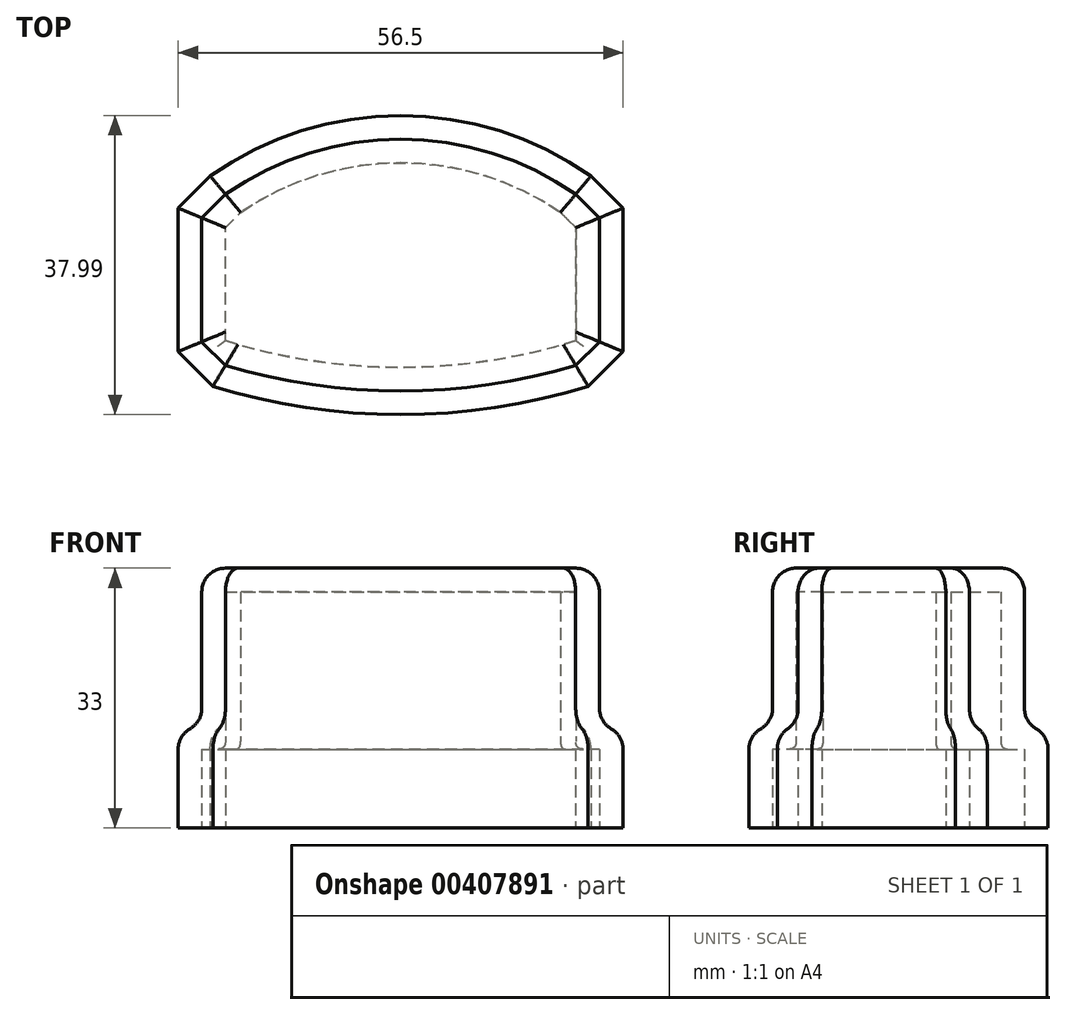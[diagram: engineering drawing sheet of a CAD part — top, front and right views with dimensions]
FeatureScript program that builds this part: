
annotation { "Feature Type Name" : "Feature", "Feature Type Description" : "" }
export const myFeature = defineFeature(function(context is Context, id is Id, definition is map)
    precondition{}
    {
        {
            var Q0;
            Q0=qCreatedBy(makeId("Top.planeOp"),FACE);
            var sketch = newSketch(context, id + "F0", { "sketchPlane" : qUnion([Q0])});
            skLineSegment(sketch, "E0.left", {"start": v(-25.25, -1.8) * mm, "end": v(-25.25, 13.94) * mm});
            skLineSegment(sketch, "E0.right", {"start": v(25.25, -1.8) * mm, "end": v(25.25, 13.94) * mm});
            skLineSegment(sketch, "E1", {"start": v(25.25, 13.94) * mm, "end": v(22.24, 16.95) * mm});
            skLineSegment(sketch, "E2", {"start": v(25.25, -1.8) * mm, "end": v(22.24, -4.8) * mm});
            skLineSegment(sketch, "E3", {"start": v(-25.25, 13.94) * mm, "end": v(-22.24, 16.95) * mm});
            skLineSegment(sketch, "E4", {"start": v(-25.25, -1.8) * mm, "end": v(-22.24, -4.8) * mm});
            skArc(sketch, "E5", {"start": v(22.24, 16.95) * mm, "mid": v(0, 23.94) * mm, "end": v(-22.24, 16.95) * mm});
            skArc(sketch, "E6", {"start": v(-22.24, -4.8) * mm, "mid": v(0, -8.05) * mm, "end": v(22.24, -4.8) * mm});
            skLineSegment(sketch, "E7", {"start": v(-25.25, -1.8) * mm, "end": v(25.25, -1.8) * mm, "construction": true});
            skLineSegment(sketch, "E8", {"start": v(-25.25, 13.94) * mm, "end": v(25.25, 13.94) * mm, "construction": true});
            skLineSegment(sketch, "E9.0", {"start": v(28.25, 15.19) * mm, "end": v(24.18, 19.25) * mm});
            skLineSegment(sketch, "E9.1", {"start": v(28.25, -3.04) * mm, "end": v(28.25, 15.19) * mm});
            skArc(sketch, "E9.2", {"start": v(24.18, 19.25) * mm, "mid": v(0, 26.94) * mm, "end": v(-24.18, 19.25) * mm});
            skLineSegment(sketch, "E9.3", {"start": v(28.25, -3.04) * mm, "end": v(23.83, -7.45) * mm});
            skLineSegment(sketch, "E9.4", {"start": v(-28.25, 15.19) * mm, "end": v(-24.18, 19.25) * mm});
            skLineSegment(sketch, "E9.5", {"start": v(-28.25, -3.04) * mm, "end": v(-28.25, 15.19) * mm});
            skLineSegment(sketch, "E9.6", {"start": v(-28.25, -3.04) * mm, "end": v(-23.83, -7.45) * mm});
            skArc(sketch, "E9.7", {"start": v(-23.83, -7.45) * mm, "mid": v(0, -11.05) * mm, "end": v(23.83, -7.45) * mm});
            skLineSegment(sketch, "E10.0", {"start": v(22.25, 12.7) * mm, "end": v(20.31, 14.64) * mm});
            skLineSegment(sketch, "E10.1", {"start": v(-22.25, 12.7) * mm, "end": v(-20.31, 14.64) * mm});
            skLineSegment(sketch, "E10.2", {"start": v(-22.25, -1.66) * mm, "end": v(-22.25, 12.7) * mm});
            skArc(sketch, "E10.3", {"start": v(20.31, 14.64) * mm, "mid": v(0, 20.94) * mm, "end": v(-20.31, 14.64) * mm});
            skArc(sketch, "E10.4", {"start": v(-22.25, -1.66) * mm, "mid": v(0, -5.05) * mm, "end": v(22.25, -1.66) * mm});
            skLineSegment(sketch, "E10.5", {"start": v(22.25, -1.66) * mm, "end": v(22.25, 12.7) * mm});
            skSolve(sketch);
        }
        {
            var Q0;
            Q0=makeQuery(id+"F0.imprint","IMPRINT",FACE,{"disambiguationData":[TD([[makeQuery(id+"F0.imprint","IMPRINT",EDGE,{"derivedFrom":sQuery(id+"F0.wireOp",EDGE,"E0.left")}),1.0]])]});
            extrude(context, id + "F1", {"entities" : qUnion([Q0]), "depth" : 13 * mm});
        }
        {
            var Q0;
            Q0=makeQuery(id+"F0.imprint","IMPRINT",FACE,{"disambiguationData":[TD([[makeQuery(id+"F0.imprint","IMPRINT",EDGE,{"derivedFrom":sQuery(id+"F0.wireOp",EDGE,"E0.left")}),-1.0]])]});
            var Q1;
            Q1=makeQuery(id+"F0.imprint","IMPRINT",FACE,{"disambiguationData":[TD([[makeQuery(id+"F0.imprint","IMPRINT",EDGE,{"derivedFrom":sQuery(id+"F0.wireOp",EDGE,"E10.0")}),1.0]])]});
            extrude(context, id + "F2", {"entities" : qUnion([Q0, Q1]), "operationType" : NewBodyOperationType.ADD, "depth" : 33 * mm});
        }
        {
            var Q0;
            Q0=makeQuery(id+"F0.imprint","IMPRINT",FACE,{"disambiguationData":[TD([[makeQuery(id+"F0.imprint","IMPRINT",EDGE,{"derivedFrom":sQuery(id+"F0.wireOp",EDGE,"E10.0")}),1.0]])]});
            var Q1;
            Q1=makeQuery(id+"F0.imprint","IMPRINT",FACE,{"disambiguationData":[TD([[makeQuery(id+"F0.imprint","IMPRINT",EDGE,{"derivedFrom":sQuery(id+"F0.wireOp",EDGE,"E0.left")}),-1.0]])]});
            extrude(context, id + "F3", {"entities" : qUnion([Q0, Q1]), "operationType" : NewBodyOperationType.REMOVE, "depth" : 10 * mm});
        }
        {
            var Q0;
            Q0=makeQuery(id+"F0.imprint","IMPRINT",FACE,{"disambiguationData":[TD([[makeQuery(id+"F0.imprint","IMPRINT",EDGE,{"derivedFrom":sQuery(id+"F0.wireOp",EDGE,"E10.0")}),1.0]])]});
            extrude(context, id + "F4", {"entities" : qUnion([Q0]), "operationType" : NewBodyOperationType.REMOVE, "depth" : 30 * mm});
        }
        {
            var Q0;
            Q0=makeQuery(id+"F1.opExtrude","CAP_EDGE",EDGE,{"disambiguationData":[OSD([sQuery(id+"F0.wireOp",EDGE,"E9.2")])],"isStart":false});
            var Q1;
            Q1=makeQuery(id+"F1.opExtrude","CAP_EDGE",EDGE,{"disambiguationData":[OSD([sQuery(id+"F0.wireOp",EDGE,"E9.4")])],"isStart":false});
            var Q2;
            Q2=makeQuery(id+"F1.opExtrude","CAP_EDGE",EDGE,{"disambiguationData":[OSD([sQuery(id+"F0.wireOp",EDGE,"E9.5")])],"isStart":false});
            var Q3;
            Q3=makeQuery(id+"F1.opExtrude","CAP_EDGE",EDGE,{"disambiguationData":[OSD([sQuery(id+"F0.wireOp",EDGE,"E9.6")])],"isStart":false});
            var Q4;
            Q4=makeQuery(id+"F1.opExtrude","CAP_EDGE",EDGE,{"disambiguationData":[OSD([sQuery(id+"F0.wireOp",EDGE,"E9.7")])],"isStart":false});
            var Q5;
            Q5=makeQuery(id+"F1.opExtrude","CAP_EDGE",EDGE,{"disambiguationData":[OSD([sQuery(id+"F0.wireOp",EDGE,"E9.0")])],"isStart":false});
            var Q6;
            Q6=makeQuery(id+"F1.opExtrude","CAP_EDGE",EDGE,{"disambiguationData":[OSD([sQuery(id+"F0.wireOp",EDGE,"E9.1")])],"isStart":false});
            var Q7;
            Q7=makeQuery(id+"F1.opExtrude","CAP_EDGE",EDGE,{"disambiguationData":[OSD([sQuery(id+"F0.wireOp",EDGE,"E9.3")])],"isStart":false});
            fillet(context, id + "F5", {"entities" : qUnion([Q0, Q1, Q2, Q3, Q4, Q5, Q6, Q7]), "radius" : 3 * mm, "tangentPropagation" : true, "allowEdgeOverflow" : false});
        }
        {
            var Q0;
            Q0=makeQuery(id+"F5.opFillet","BLEND_EDGE",EDGE,{"blendedFrom":[makeQuery(id+"F1.opExtrude","CAP_EDGE",EDGE,{"disambiguationData":[OSD([sQuery(id+"F0.wireOp",EDGE,"E9.7")])],"isStart":false}),makeQuery(id+"F2.opExtrude","SWEPT_FACE",FACE,{"disambiguationData":[OSD([sQuery(id+"F0.wireOp",EDGE,"E6")])]})],"blendedInto":[makeQuery(id+"F2.opExtrude","SWEPT_FACE",FACE,{"disambiguationData":[OSD([sQuery(id+"F0.wireOp",EDGE,"E6")])]})]});
            var Q1;
            Q1=makeQuery(id+"F5.opFillet","BLEND_EDGE",EDGE,{"blendedFrom":[makeQuery(id+"F1.opExtrude","CAP_EDGE",EDGE,{"disambiguationData":[OSD([sQuery(id+"F0.wireOp",EDGE,"E9.6")])],"isStart":false}),makeQuery(id+"F2.opExtrude","SWEPT_FACE",FACE,{"disambiguationData":[OSD([sQuery(id+"F0.wireOp",EDGE,"E4")])]})],"blendedInto":[makeQuery(id+"F2.opExtrude","SWEPT_FACE",FACE,{"disambiguationData":[OSD([sQuery(id+"F0.wireOp",EDGE,"E4")])]})]});
            var Q2;
            Q2=makeQuery(id+"F5.opFillet","BLEND_EDGE",EDGE,{"blendedFrom":[makeQuery(id+"F1.opExtrude","CAP_EDGE",EDGE,{"disambiguationData":[OSD([sQuery(id+"F0.wireOp",EDGE,"E9.5")])],"isStart":false}),makeQuery(id+"F2.opExtrude","SWEPT_FACE",FACE,{"disambiguationData":[OSD([sQuery(id+"F0.wireOp",EDGE,"E0.left")])]})],"blendedInto":[makeQuery(id+"F2.opExtrude","SWEPT_FACE",FACE,{"disambiguationData":[OSD([sQuery(id+"F0.wireOp",EDGE,"E0.left")])]})]});
            var Q3;
            Q3=makeQuery(id+"F5.opFillet","BLEND_EDGE",EDGE,{"blendedFrom":[makeQuery(id+"F1.opExtrude","CAP_EDGE",EDGE,{"disambiguationData":[OSD([sQuery(id+"F0.wireOp",EDGE,"E9.3")])],"isStart":false}),makeQuery(id+"F2.opExtrude","SWEPT_FACE",FACE,{"disambiguationData":[OSD([sQuery(id+"F0.wireOp",EDGE,"E2")])]})],"blendedInto":[makeQuery(id+"F2.opExtrude","SWEPT_FACE",FACE,{"disambiguationData":[OSD([sQuery(id+"F0.wireOp",EDGE,"E2")])]})]});
            var Q4;
            Q4=makeQuery(id+"F5.opFillet","BLEND_EDGE",EDGE,{"blendedFrom":[makeQuery(id+"F1.opExtrude","CAP_EDGE",EDGE,{"disambiguationData":[OSD([sQuery(id+"F0.wireOp",EDGE,"E9.1")])],"isStart":false}),makeQuery(id+"F2.opExtrude","SWEPT_FACE",FACE,{"disambiguationData":[OSD([sQuery(id+"F0.wireOp",EDGE,"E0.right")])]})],"blendedInto":[makeQuery(id+"F2.opExtrude","SWEPT_FACE",FACE,{"disambiguationData":[OSD([sQuery(id+"F0.wireOp",EDGE,"E0.right")])]})]});
            var Q5;
            Q5=makeQuery(id+"F5.opFillet","BLEND_EDGE",EDGE,{"blendedFrom":[makeQuery(id+"F1.opExtrude","CAP_EDGE",EDGE,{"disambiguationData":[OSD([sQuery(id+"F0.wireOp",EDGE,"E9.0")])],"isStart":false}),makeQuery(id+"F2.opExtrude","SWEPT_FACE",FACE,{"disambiguationData":[OSD([sQuery(id+"F0.wireOp",EDGE,"E1")])]})],"blendedInto":[makeQuery(id+"F2.opExtrude","SWEPT_FACE",FACE,{"disambiguationData":[OSD([sQuery(id+"F0.wireOp",EDGE,"E1")])]})]});
            var Q6;
            Q6=makeQuery(id+"F5.opFillet","BLEND_EDGE",EDGE,{"blendedFrom":[makeQuery(id+"F1.opExtrude","CAP_EDGE",EDGE,{"disambiguationData":[OSD([sQuery(id+"F0.wireOp",EDGE,"E9.2")])],"isStart":false}),makeQuery(id+"F2.opExtrude","SWEPT_FACE",FACE,{"disambiguationData":[OSD([sQuery(id+"F0.wireOp",EDGE,"E5")])]})],"blendedInto":[makeQuery(id+"F2.opExtrude","SWEPT_FACE",FACE,{"disambiguationData":[OSD([sQuery(id+"F0.wireOp",EDGE,"E5")])]})]});
            var Q7;
            Q7=makeQuery(id+"F5.opFillet","BLEND_EDGE",EDGE,{"blendedFrom":[makeQuery(id+"F1.opExtrude","CAP_EDGE",EDGE,{"disambiguationData":[OSD([sQuery(id+"F0.wireOp",EDGE,"E9.4")])],"isStart":false}),makeQuery(id+"F2.opExtrude","SWEPT_FACE",FACE,{"disambiguationData":[OSD([sQuery(id+"F0.wireOp",EDGE,"E3")])]})],"blendedInto":[makeQuery(id+"F2.opExtrude","SWEPT_FACE",FACE,{"disambiguationData":[OSD([sQuery(id+"F0.wireOp",EDGE,"E3")])]})]});
            fillet(context, id + "F6", {"entities" : qUnion([Q0, Q1, Q2, Q3, Q4, Q5, Q6, Q7]), "radius" : 3 * mm, "tangentPropagation" : true, "allowEdgeOverflow" : false});
        }
        {
            var Q0;
            Q0=makeQuery(id+"F2.opExtrude","CAP_EDGE",EDGE,{"disambiguationData":[OSD([sQuery(id+"F0.wireOp",EDGE,"E6")])],"isStart":false});
            var Q1;
            Q1=makeQuery(id+"F2.opExtrude","CAP_FACE",FACE,{"disambiguationData":[OSD([sQuery(id+"F0.wireOp",EDGE,"E0.left"),sQuery(id+"F0.wireOp",EDGE,"E0.right"),sQuery(id+"F0.wireOp",EDGE,"E1"),sQuery(id+"F0.wireOp",EDGE,"E2"),sQuery(id+"F0.wireOp",EDGE,"E3"),sQuery(id+"F0.wireOp",EDGE,"E4"),sQuery(id+"F0.wireOp",EDGE,"E5"),sQuery(id+"F0.wireOp",EDGE,"E6")])],"isStart":false});
            fillet(context, id + "F7", {"entities" : qUnion([Q0, Q1]), "radius" : 3 * mm, "tangentPropagation" : true, "allowEdgeOverflow" : false});
        }
        {
            var Q0;
            Q0=makeQuery(id+"F4.boolean.opBoolean","INTERSECT",EDGE,{"derivedFrom":[makeQuery(id+"F3.boolean.opBoolean","COPY",FACE,{"derivedFrom":makeQuery(id+"F3.opExtrude","CAP_FACE",FACE,{"disambiguationData":[OSD([sQuery(id+"F0.wireOp",EDGE,"E0.left"),sQuery(id+"F0.wireOp",EDGE,"E0.right"),sQuery(id+"F0.wireOp",EDGE,"E1"),sQuery(id+"F0.wireOp",EDGE,"E2"),sQuery(id+"F0.wireOp",EDGE,"E3"),sQuery(id+"F0.wireOp",EDGE,"E4"),sQuery(id+"F0.wireOp",EDGE,"E5"),sQuery(id+"F0.wireOp",EDGE,"E6")])],"isStart":false})}),makeQuery(id+"F4.opExtrude","SWEPT_FACE",FACE,{"disambiguationData":[OSD([sQuery(id+"F0.wireOp",EDGE,"E10.5")])]})]});
            var Q1;
            Q1=makeQuery(id+"F4.boolean.opBoolean","INTERSECT",EDGE,{"derivedFrom":[makeQuery(id+"F3.boolean.opBoolean","COPY",FACE,{"derivedFrom":makeQuery(id+"F3.opExtrude","CAP_FACE",FACE,{"disambiguationData":[OSD([sQuery(id+"F0.wireOp",EDGE,"E0.left"),sQuery(id+"F0.wireOp",EDGE,"E0.right"),sQuery(id+"F0.wireOp",EDGE,"E1"),sQuery(id+"F0.wireOp",EDGE,"E2"),sQuery(id+"F0.wireOp",EDGE,"E3"),sQuery(id+"F0.wireOp",EDGE,"E4"),sQuery(id+"F0.wireOp",EDGE,"E5"),sQuery(id+"F0.wireOp",EDGE,"E6")])],"isStart":false})}),makeQuery(id+"F4.opExtrude","SWEPT_FACE",FACE,{"disambiguationData":[OSD([sQuery(id+"F0.wireOp",EDGE,"E10.0")])]})]});
            var Q2;
            Q2=makeQuery(id+"F4.boolean.opBoolean","INTERSECT",EDGE,{"derivedFrom":[makeQuery(id+"F3.boolean.opBoolean","COPY",FACE,{"derivedFrom":makeQuery(id+"F3.opExtrude","CAP_FACE",FACE,{"disambiguationData":[OSD([sQuery(id+"F0.wireOp",EDGE,"E0.left"),sQuery(id+"F0.wireOp",EDGE,"E0.right"),sQuery(id+"F0.wireOp",EDGE,"E1"),sQuery(id+"F0.wireOp",EDGE,"E2"),sQuery(id+"F0.wireOp",EDGE,"E3"),sQuery(id+"F0.wireOp",EDGE,"E4"),sQuery(id+"F0.wireOp",EDGE,"E5"),sQuery(id+"F0.wireOp",EDGE,"E6")])],"isStart":false})}),makeQuery(id+"F4.opExtrude","SWEPT_FACE",FACE,{"disambiguationData":[OSD([sQuery(id+"F0.wireOp",EDGE,"E10.3")])]})]});
            var Q3;
            Q3=makeQuery(id+"F4.boolean.opBoolean","INTERSECT",EDGE,{"derivedFrom":[makeQuery(id+"F3.boolean.opBoolean","COPY",FACE,{"derivedFrom":makeQuery(id+"F3.opExtrude","CAP_FACE",FACE,{"disambiguationData":[OSD([sQuery(id+"F0.wireOp",EDGE,"E0.left"),sQuery(id+"F0.wireOp",EDGE,"E0.right"),sQuery(id+"F0.wireOp",EDGE,"E1"),sQuery(id+"F0.wireOp",EDGE,"E2"),sQuery(id+"F0.wireOp",EDGE,"E3"),sQuery(id+"F0.wireOp",EDGE,"E4"),sQuery(id+"F0.wireOp",EDGE,"E5"),sQuery(id+"F0.wireOp",EDGE,"E6")])],"isStart":false})}),makeQuery(id+"F4.opExtrude","SWEPT_FACE",FACE,{"disambiguationData":[OSD([sQuery(id+"F0.wireOp",EDGE,"E10.1")])]})]});
            var Q4;
            Q4=makeQuery(id+"F4.boolean.opBoolean","INTERSECT",EDGE,{"derivedFrom":[makeQuery(id+"F3.boolean.opBoolean","COPY",FACE,{"derivedFrom":makeQuery(id+"F3.opExtrude","CAP_FACE",FACE,{"disambiguationData":[OSD([sQuery(id+"F0.wireOp",EDGE,"E0.left"),sQuery(id+"F0.wireOp",EDGE,"E0.right"),sQuery(id+"F0.wireOp",EDGE,"E1"),sQuery(id+"F0.wireOp",EDGE,"E2"),sQuery(id+"F0.wireOp",EDGE,"E3"),sQuery(id+"F0.wireOp",EDGE,"E4"),sQuery(id+"F0.wireOp",EDGE,"E5"),sQuery(id+"F0.wireOp",EDGE,"E6")])],"isStart":false})}),makeQuery(id+"F4.opExtrude","SWEPT_FACE",FACE,{"disambiguationData":[OSD([sQuery(id+"F0.wireOp",EDGE,"E10.2")])]})]});
            var Q5;
            Q5=makeQuery(id+"F4.boolean.opBoolean","INTERSECT",EDGE,{"derivedFrom":[makeQuery(id+"F3.boolean.opBoolean","COPY",FACE,{"derivedFrom":makeQuery(id+"F3.opExtrude","CAP_FACE",FACE,{"disambiguationData":[OSD([sQuery(id+"F0.wireOp",EDGE,"E0.left"),sQuery(id+"F0.wireOp",EDGE,"E0.right"),sQuery(id+"F0.wireOp",EDGE,"E1"),sQuery(id+"F0.wireOp",EDGE,"E2"),sQuery(id+"F0.wireOp",EDGE,"E3"),sQuery(id+"F0.wireOp",EDGE,"E4"),sQuery(id+"F0.wireOp",EDGE,"E5"),sQuery(id+"F0.wireOp",EDGE,"E6")])],"isStart":false})}),makeQuery(id+"F4.opExtrude","SWEPT_FACE",FACE,{"disambiguationData":[OSD([sQuery(id+"F0.wireOp",EDGE,"E10.4")])]})]});
            fillet(context, id + "F8", {"entities" : qUnion([Q0, Q1, Q2, Q3, Q4, Q5]), "radius" : 1 * mm, "tangentPropagation" : true, "rho" : 0.5, "crossSection" : FilletCrossSection.CONIC, "allowEdgeOverflow" : false});
        }
    });
